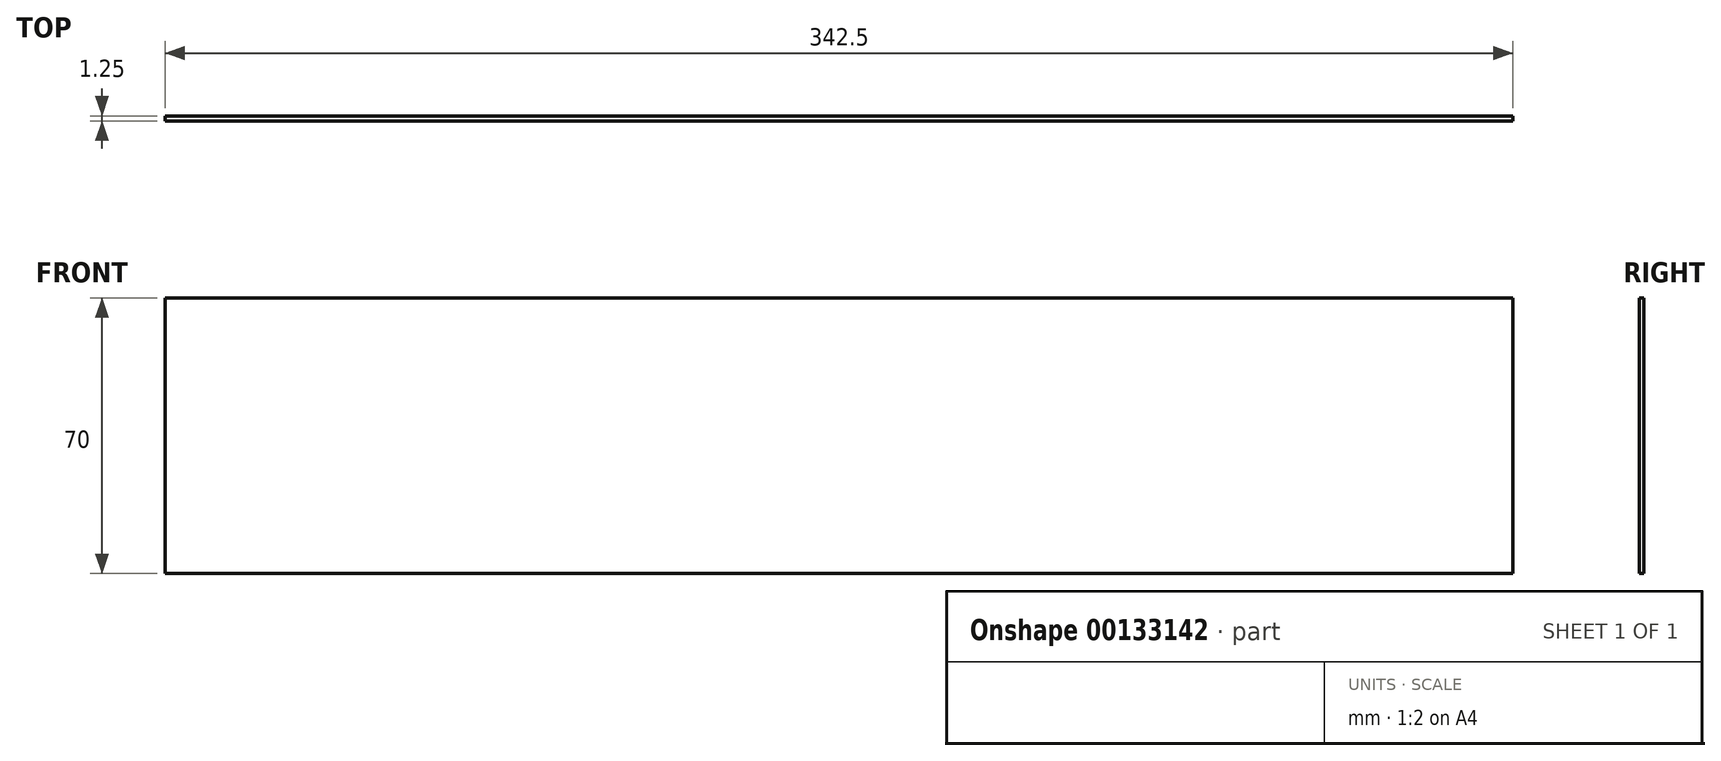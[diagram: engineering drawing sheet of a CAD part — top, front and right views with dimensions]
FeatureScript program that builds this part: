
annotation { "Feature Type Name" : "Feature", "Feature Type Description" : "" }
export const myFeature = defineFeature(function(context is Context, id is Id, definition is map)
    precondition{}
    {
        {
            var Q0;
            Q0=qCreatedBy(makeId("Front.planeOp"),FACE);
            var sketch = newSketch(context, id + "F0", { "sketchPlane" : qUnion([Q0])});
            skLineSegment(sketch, "E0.bottom", {"start": v(-171.25, 35) * mm, "end": v(171.25, 35) * mm});
            skLineSegment(sketch, "E0.top", {"start": v(-171.25, -35) * mm, "end": v(171.25, -35) * mm});
            skLineSegment(sketch, "E0.left", {"start": v(-171.25, 35) * mm, "end": v(-171.25, -35) * mm});
            skLineSegment(sketch, "E0.right", {"start": v(171.25, 35) * mm, "end": v(171.25, -35) * mm});
            skPoint(sketch, "E0.middle", {"position": v(0, 0) * mm});
            skSolve(sketch);
        }
        {
            var Q0;
            Q0=makeQuery(id+"F0.imprint","IMPRINT",FACE,{"disambiguationData":[TD([[makeQuery(id+"F0.imprint","IMPRINT",EDGE,{"derivedFrom":sQuery(id+"F0.wireOp",EDGE,"E0.bottom")}),-1.0]])]});
            extrude(context, id + "F1", {"entities" : qUnion([Q0]), "depth" : 1.25 * mm});
        }
    });
